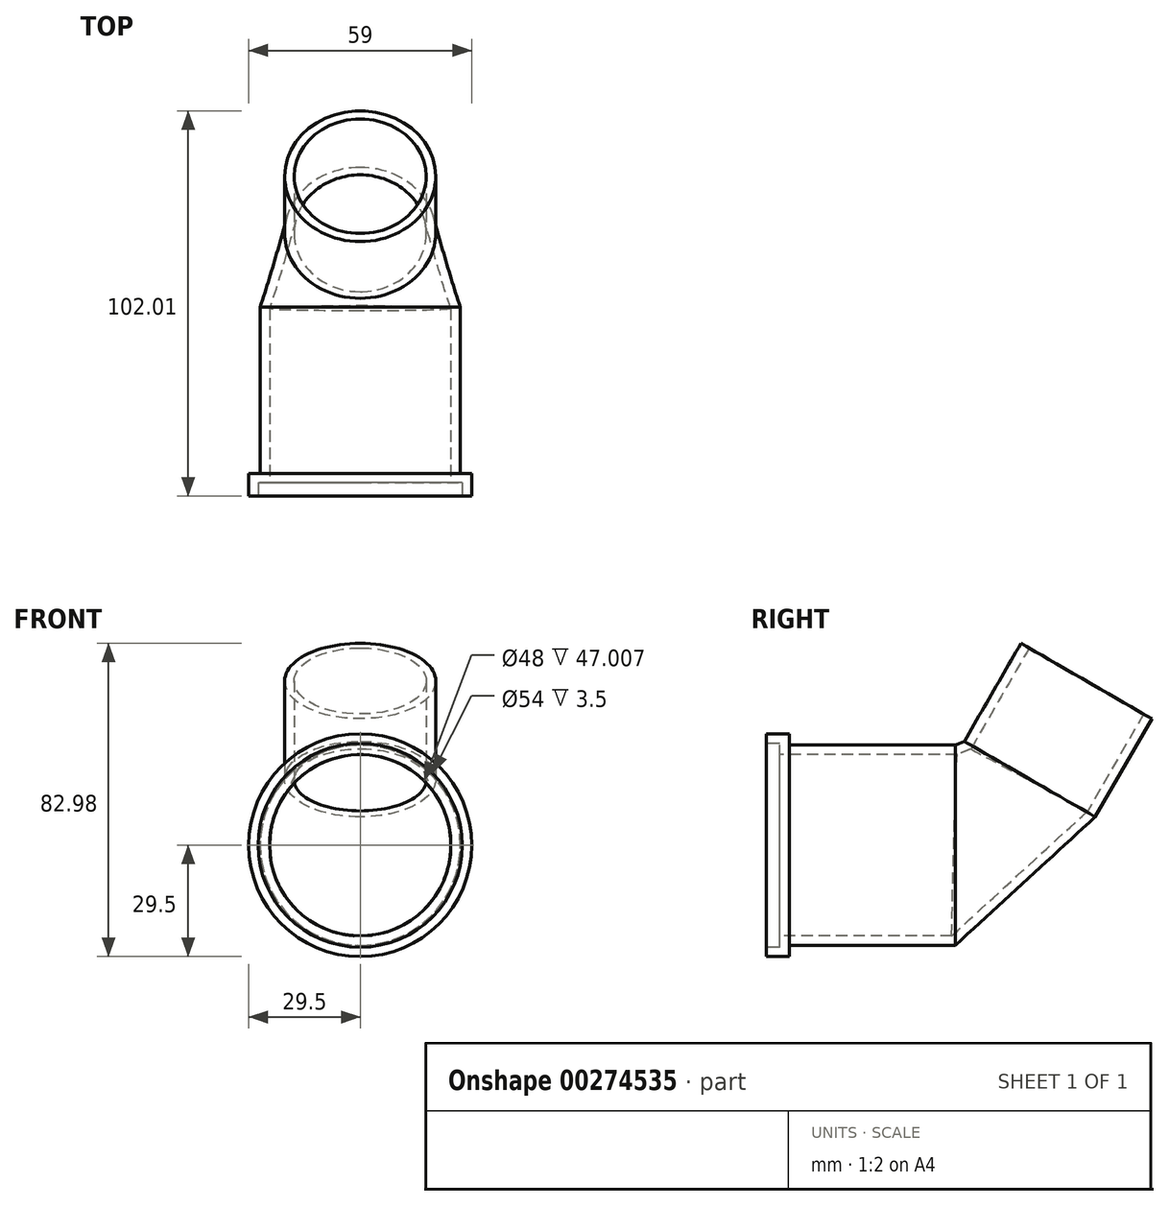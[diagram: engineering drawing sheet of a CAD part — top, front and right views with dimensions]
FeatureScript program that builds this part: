
annotation { "Feature Type Name" : "Feature", "Feature Type Description" : "" }
export const myFeature = defineFeature(function(context is Context, id is Id, definition is map)
    precondition{}
    {
        {
            var Q0;
            Q0=qCreatedBy(makeId("Front.planeOp"),FACE);
            var sketch = newSketch(context, id + "F0", { "sketchPlane" : qUnion([Q0])});
            skCircle(sketch, "E0", {"center": v(0, 0) * mm, "radius": 29.5 * mm});
            skCircle(sketch, "E1", {"center": v(0, 0) * mm, "radius": 26.5 * mm});
            skSolve(sketch);
        }
        {
            var Q0;
            Q0=makeQuery(id+"F0.imprint","IMPRINT",FACE,{"disambiguationData":[TD([[makeQuery(id+"F0.imprint","IMPRINT",EDGE,{"derivedFrom":sQuery(id+"F0.wireOp",EDGE,"E1")}),1.0]])]});
            extrude(context, id + "F1", {"entities" : qUnion([Q0]), "oppositeDirection" : true, "depth" : 50 * mm});
        }
        {
            var Q0;
            Q0=makeQuery(id+"F0.imprint","IMPRINT",FACE,{"disambiguationData":[TD([[makeQuery(id+"F0.imprint","IMPRINT",EDGE,{"derivedFrom":sQuery(id+"F0.wireOp",EDGE,"E0")}),1.0]])]});
            extrude(context, id + "F2", {"entities" : qUnion([Q0]), "operationType" : NewBodyOperationType.ADD, "oppositeDirection" : true, "depth" : 6 * mm});
        }
        {
            var Q0;
            Q0=qCreatedBy(makeId("Top.planeOp"),FACE);
            var sketch = newSketch(context, id + "F3", { "sketchPlane" : qUnion([Q0])});
            skLineSegment(sketch, "E2", {"start": v(-78.04, 100) * mm, "end": v(80.67, 100) * mm});
            skSolve(sketch);
        }
        {
            var Q0;
            Q0=sQuery(id+"F3.wireOp",EDGE,"E2");
            cPlane(context, id + "F4", {"entities" : qUnion([Q0]), "cplaneType" : CPlaneType.LINE_ANGLE, "offset" : 25 * mm, "angle" : 60 * degree, "width" : 150 * mm, "height" : 150 * mm});
        }
        {
            var Q0;
            Q0=qCreatedBy(id+"F4.planeOp",FACE);
            var sketch = newSketch(context, id + "F5", { "sketchPlane" : qUnion([Q0])});
            skCircle(sketch, "E3", {"center": v(0, 51.6) * mm, "radius": 20 * mm});
            skSolve(sketch);
        }
        {
            var Q0;
            Q0=makeQuery(id+"F5.imprint","IMPRINT",FACE,{"disambiguationData":[TD([[makeQuery(id+"F5.imprint","IMPRINT",EDGE,{"derivedFrom":sQuery(id+"F5.wireOp",EDGE,"E3")}),1.0]])]});
            extrude(context, id + "F6", {"entities" : qUnion([Q0]), "depth" : 30 * mm});
        }
        {
            var Q0;
            Q0=makeQuery(id+"F1.opExtrude","CAP_FACE",FACE,{"disambiguationData":[OSD([sQuery(id+"F0.wireOp",EDGE,"E1")])],"isStart":false});
            var Q1;
            Q1=makeQuery(id+"F6.opExtrude","CAP_FACE",FACE,{"disambiguationData":[OSD([sQuery(id+"F5.wireOp",EDGE,"E3")])],"isStart":true});
            loft(context, id + "F7", {"operationType" : NewBodyOperationType.ADD, "sheetProfilesArray" : [{ "sheetProfileEntities" : qUnion([Q0]) }, { "sheetProfileEntities" : qUnion([Q1]) }]});
        }
        {
            var Q0;
            Q0=makeQuery(id+"F6.opExtrude","CAP_FACE",FACE,{"disambiguationData":[OSD([sQuery(id+"F5.wireOp",EDGE,"E3")])],"isStart":false});
            var Q1;
            {var subQ0=sQuery(id+"F0.wireOp",EDGE,"E1");Q1=makeQuery(id+"F2.boolean.opBoolean","MERGE",FACE,{"derivedFrom":[makeQuery(id+"F1.opExtrude","CAP_FACE",FACE,{"disambiguationData":[OSD([subQ0])],"isStart":true}),makeQuery(id+"F2.opExtrude","CAP_FACE",FACE,{"disambiguationData":[OSD([sQuery(id+"F0.wireOp",EDGE,"E0"),subQ0])],"isStart":true})]});}
            shell(context, id + "F8", {"entities" : qUnion([Q0, Q1]), "thickness" : 2.5 * mm});
        }
    });
